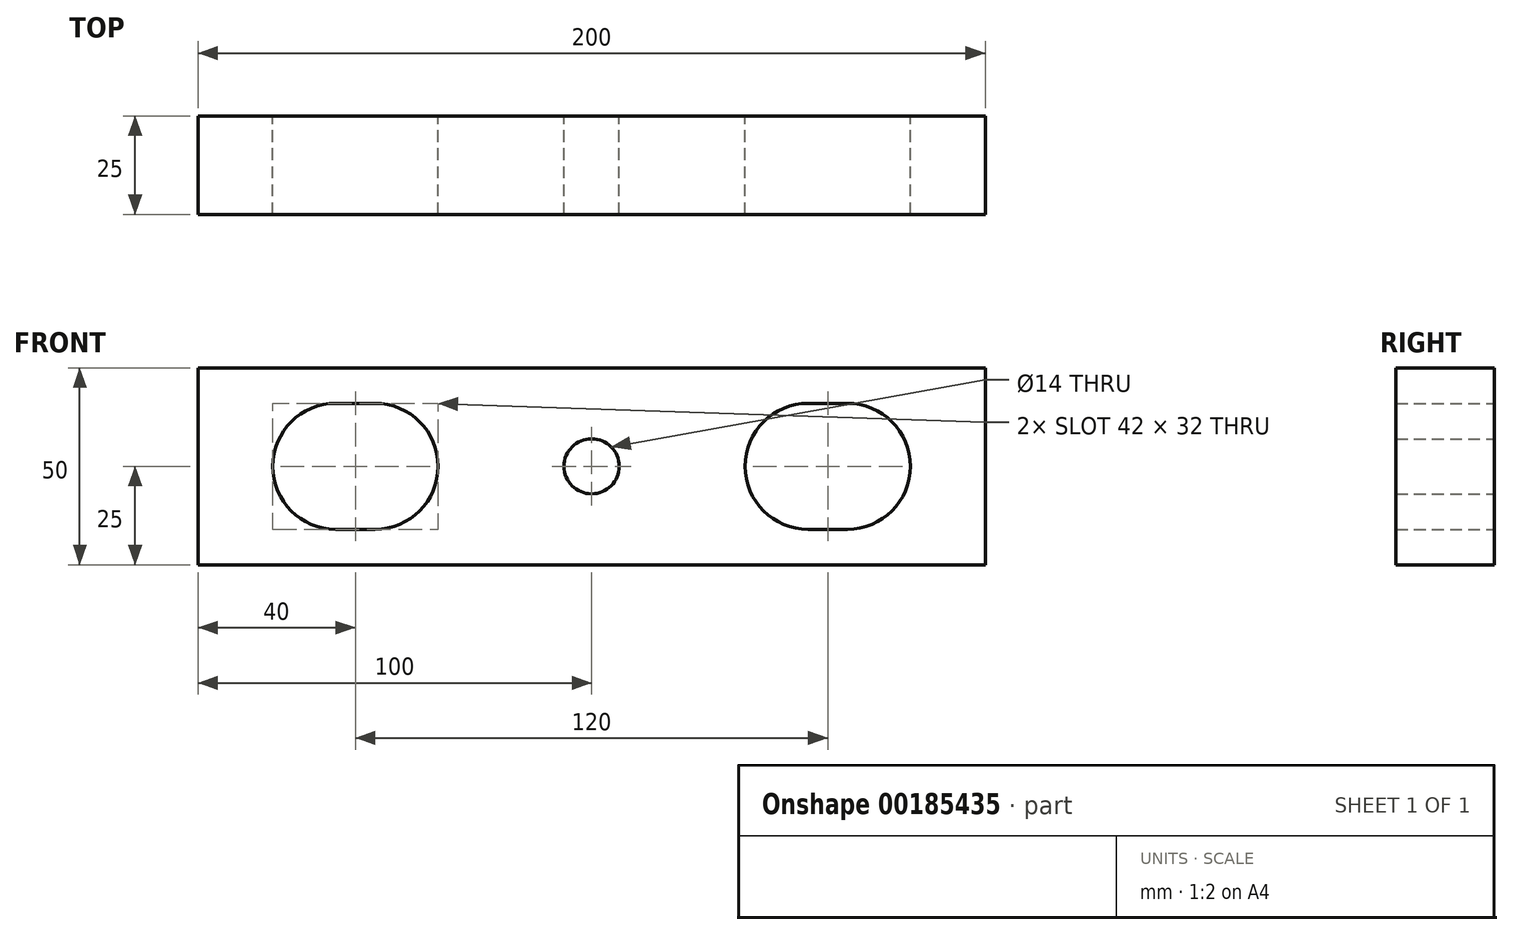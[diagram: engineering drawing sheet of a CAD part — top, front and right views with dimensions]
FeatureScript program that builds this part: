
annotation { "Feature Type Name" : "Feature", "Feature Type Description" : "" }
export const myFeature = defineFeature(function(context is Context, id is Id, definition is map)
    precondition{}
    {
        {
            var Q0;
            Q0=qCreatedBy(makeId("Front.planeOp"),FACE);
            var sketch = newSketch(context, id + "F0", { "sketchPlane" : qUnion([Q0])});
            skLineSegment(sketch, "E0.bottom", {"start": v(-100, 0) * mm, "end": v(100, 0) * mm});
            skLineSegment(sketch, "E0.top", {"start": v(-100, -50) * mm, "end": v(100, -50) * mm});
            skLineSegment(sketch, "E0.left", {"start": v(-100, 0) * mm, "end": v(-100, -50) * mm});
            skLineSegment(sketch, "E0.right", {"start": v(100, 0) * mm, "end": v(100, -50) * mm});
            skLineSegment(sketch, "E1", {"start": v(-65, -25) * mm, "end": v(-55, -25) * mm});
            skLineSegment(sketch, "E2", {"start": v(0, -50) * mm, "end": v(0, 0) * mm, "construction": true});
            skLineSegment(sketch, "E3.MirrorCS", {"start": v(65, -25) * mm, "end": v(55, -25) * mm});
            skArc(sketch, "E4.0.startCap", {"start": v(-65, -41) * mm, "mid": v(-81, -25) * mm, "end": v(-65, -9) * mm});
            skArc(sketch, "E4.0.endCap", {"start": v(-55, -9) * mm, "mid": v(-39, -25) * mm, "end": v(-55, -41) * mm});
            skLineSegment(sketch, "E4.0.left", {"start": v(-65, -9) * mm, "end": v(-55, -9) * mm});
            skLineSegment(sketch, "E4.0.right", {"start": v(-65, -41) * mm, "end": v(-55, -41) * mm});
            skArc(sketch, "E5.0.startCap", {"start": v(65, -9) * mm, "mid": v(81, -25) * mm, "end": v(65, -41) * mm});
            skArc(sketch, "E5.0.endCap", {"start": v(55, -41) * mm, "mid": v(39, -25) * mm, "end": v(55, -9) * mm});
            skLineSegment(sketch, "E5.0.left", {"start": v(65, -41) * mm, "end": v(55, -41) * mm});
            skLineSegment(sketch, "E5.0.right", {"start": v(65, -9) * mm, "end": v(55, -9) * mm});
            skPoint(sketch, "E6", {"position": v(0, -25) * mm});
            skSolve(sketch);
        }
        {
            var Q0;
            Q0 = qSketchRegion(id + "F0", true);
            extrude(context, id + "F1", {"entities" : qUnion([Q0]), "depth" : 25 * mm});
        }
        {
            var Q0;
            Q0=sQuery(id+"F0.wireOp",VERTEX,"E6");
            var Q1;
            Q1=makeQuery(id+"F1.opExtrude","SWEPT_BODY",BODY,{"disambiguationData":[OSD([sQuery(id+"F0.wireOp",EDGE,"E0.bottom"),sQuery(id+"F0.wireOp",EDGE,"E0.top"),sQuery(id+"F0.wireOp",EDGE,"E0.left"),sQuery(id+"F0.wireOp",EDGE,"E0.right"),sQuery(id+"F0.wireOp",EDGE,"E4.0.startCap"),sQuery(id+"F0.wireOp",EDGE,"E4.0.endCap"),sQuery(id+"F0.wireOp",EDGE,"E4.0.left"),sQuery(id+"F0.wireOp",EDGE,"E4.0.right"),sQuery(id+"F0.wireOp",EDGE,"E5.0.startCap"),sQuery(id+"F0.wireOp",EDGE,"E5.0.endCap"),sQuery(id+"F0.wireOp",EDGE,"E5.0.left"),sQuery(id+"F0.wireOp",EDGE,"E5.0.right")])]});
            hole(context, id + "F2", {"style" : HoleStyle.SIMPLE, "endStyle" : HoleEndStyle.THROUGH, "oppositeDirection" : true, "standardTappedOrClearance" : lookupTablePath({ "standard" : "ISO", "engagement" : "75%", "pitch" : "2 mm", "size" : "M16", "type" : "Tapped" }), "standardBlindInLast" : lookupTablePath({ "standard" : "ISO", "engagement" : "75%", "pitch" : "2 mm", "size" : "M16", "type" : "Tapped" }), "holeDiameter" : 14 * mm, "locations" : qUnion([Q0]), "scope" : qUnion([Q1]), "isTappedThrough" : true, "majorDiameter" : 16 * mm, "showTappedDepth" : true});
        }
    });
